# Revit family: Ifö SBNK series
name_source: partatom
category: Plumbing Fixtures
revit_build: Autodesk Revit 2015 (Build: 20140606_1530(x64)
units: mm (PartAtom-declared; Revit-internal decimal feet)

## types (3) — shared parameters
Assembly Code = D2010
Brand = Ifö
Category = ShowerDoor
Color = Hardened Glass, Clear
Handle Material = Metal, Matte Silver
Handle Visibility = No
Height = 2000 mm  [stored 6.56168 ft]
Manufacturer = Geberit
ModelReference = Space
NominalHeight = 2000
Panel Material = Hardened Glass, Clear
PanelMaterial = Hardened Glass, Clear
Profile Material = Brushed Aluminum
ProfileMaterial = Brushed aluminium
Rubber Material = Rubber
Serie = Space
Shape = Curved
Type = Building element
URL = www.ifo.dk
URL.dk = http://www.ifo.dk
URL.no = http://www.ifosanitar.no
URL.se = http://www.ifo.se
ifcExportAs = IfcFurnitureType
ifcExportType = USERDEFINED
zero-valued in all types: NominalDepth

## per-type parameters (varying)
| type | Angle | BIMObjectName | CE Labeling | Features | Length | Metal Lining | Model | NominalWidth | Panel Visibility | Radius | Size | Width |
| Ifö Space SBNK 900 | 43.00° | Ifö SBNK series |  | feature1, feature2, feature97 | 304 mm | Yes | 058900090 - Ifö Space SBNK 900 | 741 mm  [stored 2.4311 ft] | No | 525 mm  [stored 1.72244 ft] | 741x2000x0 | 741 mm  [stored 2.4311 ft] |
| Ifö Space SBNK 900 H | 68.00° |  | n&a | feature1, feature2, feature96 | 463 mm | No | 058900290 - Ifö Space SBNK 900 H | 900 mm  [stored 2.95276 ft] | Yes | 400 mm  [stored 1.31234 ft] | 900x2000x0 | 900 mm  [stored 2.95276 ft] |
| Ifö Space SBNK 900 knob | 43.00° |  |  | feature1, feature2, feature95 | 304 mm | Yes | 058900090 - Ifö Space SBNK 900 | 741 mm  [stored 2.4311 ft] | No | 525 mm  [stored 1.72244 ft] | 741x2000x0 | 741 mm  [stored 2.4311 ft] |

note: column(s) folded — value = type name in every type: Description, Name

note: [stored X ft] marks values corroborated as IEEE doubles in the binary element streams (Revit-internal decimal feet)

## geometry (parser evidence)
native form markers: Blend x10, Sweep x3
no freeform markers — native parametric forms only
